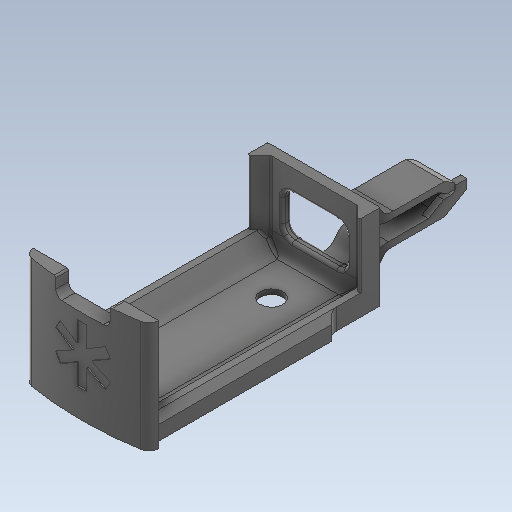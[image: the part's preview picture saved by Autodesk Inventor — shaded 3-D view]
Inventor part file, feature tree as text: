
AUTODESK INVENTOR PART (.ipt)
format: ipt  version: 2020 (Build 240168000, 168)  size: 823,808 bytes
history: native  units: mm
features: projected_geometry x32, extrude x18, sketch x16, fillet x10, other x9, chamfer x2
ambient origin geometry x8: Origin, YZ Plane, XZ Plane, XY Plane, X Axis, Y Axis, Z Axis, Center Point
bodies: Body1 (feature_tree)
feature tree (87):
  other  "Твердое тело1"
  sketch  "Эскиз1"
  extrude  "Выдавливание3"  Depth=202.0mm
  other  "РабПлоскость1"
  extrude  "Выдавливание1"  Depth=35.0mm
  other  "РабПлоскость2"
  sketch  "Эскиз2"
  extrude  "Выдавливание4"  Depth=68.0mm
  extrude  "Выдавливание5"  Depth=2.0mm
  sketch  "Эскиз4"
  extrude  "Выдавливание6"  Depth=2.0mm
  extrude  "Выдавливание7"  Depth=3.0mm
  other  "РабПлоскость3"
  extrude  "Выдавливание8"  Depth=3.0mm
  other  "РабПлоскость4"
  extrude  "Выдавливание9"  Depth=210.0mm
  sketch  "Эскиз8"
  extrude  "Выдавливание10"  Depth=20.0mm TaperAngle=0.0deg
  fillet  "Сопряжение1"  Radius=1.5mm
  fillet  "Сопряжение2"  Radius=28.0mm
  fillet  "Сопряжение3"  Radius=7.0mm
  fillet  "Сопряжение4"  Radius=20.0mm
  fillet  "Сопряжение5"  Radius=13.0mm
  extrude  "Выдавливание11"  Depth=5.0mm
  extrude  "Выдавливание12"  Depth=3.0mm
  fillet  "Сопряжение6"  Radius=10.0mm
  extrude  "Выдавливание13"  Depth=84.0mm
  chamfer  "Фаска1"  Distance=5.0mm
  fillet  "Сопряжение7"  Radius=52.0mm
  sketch  "Эскиз10"
  other  "РабПлоскость5"
  extrude  "Выдавливание14"  Depth=5.0mm TaperAngle=0.0deg
  fillet  "Сопряжение8"  Radius=35.0mm
  extrude  "Выдавливание15"  Depth=18.0mm
  fillet  "Сопряжение9"  Radius=3.0mm
  extrude  "Выдавливание16"  Depth=30.0mm TaperAngle=360.0deg
  fillet  "Сопряжение10"  Radius=0.5mm
  extrude  "Выдавливание17"  TaperAngle=0.0deg  [1 undecoded]
  chamfer  "Фаска2"  Distance=8.0mm
  other  "РабПлоскость10"
  other  "РабПлоскость9"
  sketch  "Эскиз14"
  other  "РабПлоскость8"
  sketch  "Эскиз15"
  sketch  "Эскиз16"
  sketch  "Эскиз17"
  extrude  "Выдавливание20"  Depth=2.0mm
  extrude  "Выдавливание21"  Depth=1.5mm TaperAngle=0.0deg
  projected_geometry  "Спроецированная петля1"
  projected_geometry  "Спроецированная петля7"
  projected_geometry  "Спроецированная петля8"
  sketch  "Эскиз3"
  projected_geometry  "Спроецированная петля9"
  projected_geometry  "Спроецированная петля10"
  projected_geometry  "Спроецированная петля11"
  projected_geometry  "Спроецированная петля12"
  sketch  "Эскиз5"
  projected_geometry  "Спроецированная петля13"
  projected_geometry  "Спроецированная петля14"
  projected_geometry  "Спроецированная петля15"
  projected_geometry  "Спроецированная петля16"
  projected_geometry  "Спроецированная петля17"
  sketch  "Эскиз6"
  projected_geometry  "Спроецированная петля18"
  projected_geometry  "Спроецированная петля19"
  projected_geometry  "Спроецированная петля20"
  projected_geometry  "Спроецированная петля21"
  projected_geometry  "Спроецированная петля22"
  projected_geometry  "Спроецированная петля23"
  projected_geometry  "Спроецированная петля24"
  projected_geometry  "Спроецированная петля25"
  projected_geometry  "Спроецированная петля26"
  projected_geometry  "Спроецированная петля27"
  projected_geometry  "Спроецированная петля28"
  sketch  "Эскиз9"
  projected_geometry  "Спроецированная петля29"
  projected_geometry  "Спроецированная петля30"
  sketch  "Эскиз11"
  projected_geometry  "Спроецированная петля31"
  projected_geometry  "Спроецированная петля32"
  projected_geometry  "Спроецированная петля33"
  sketch  "Эскиз12"
  projected_geometry  "Спроецированная петля34"
  projected_geometry  "Спроецированная петля35"
  projected_geometry  "Спроецированная петля37"
  sketch  "Эскиз18"
  projected_geometry  "Спроецированная петля38"
note: 1 required parameter value undecoded (feature->parameter linkage not recoverable at this tier; creation-order binding heuristic only, values carry confidence <= 0.55)
